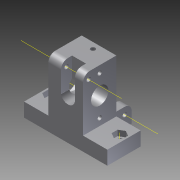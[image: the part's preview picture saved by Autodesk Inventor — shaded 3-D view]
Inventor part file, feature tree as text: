
AUTODESK INVENTOR PART (.ipt)
format: ipt  version: 2012 (Build 160160000, 160)  size: 299,008 bytes
history: native  units: mm
features: hole x11, sketch x10, extrude x7, other x4, fillet x2, plane x1, projected_geometry x1
ambient origin geometry x8: Origin, YZ Plane, XZ Plane, XY Plane, X Axis, Y Axis, Z Axis, Center Point
bodies: Solid1 (feature_tree)
feature tree (36):
  extrude  "Extrusion1"  Depth=24.0mm
  hole  "Hole1"  [1 undecoded]
  hole  "Hole2"  [1 undecoded]
  other  "Work Axis1"
  other  "Work Axis2"
  extrude  "Extrusion2"  Depth=7.5mm
  hole  "Hole3"  [1 undecoded]
  hole  "Hole4"  [1 undecoded]
  extrude  "Extrusion3"  Depth=6.0mm
  hole  "Hole5"  [1 undecoded]
  fillet  "Fillet1"  Radius=12.5mm
  extrude  "Extrusion4"  Depth=13.0mm
  hole  "Hole6"  [1 undecoded]
  hole  "Hole7"  [1 undecoded]
  hole  "Hole8"  [1 undecoded]
  hole  "Hole9"  [1 undecoded]
  hole  "Hole10"  [1 undecoded]
  plane  "Work Plane1"
  extrude  "Extrusion5"  Depth=3.0mm
  extrude  "Extrusion6"  Depth=19.0mm
  extrude  "Extrusion7"  [1 undecoded]
  hole  "Hole11"  [1 undecoded]
  sketch  "Sketch11"  dims[d46=11.0mm d47=25.0mm d48=12.5mm d49=13.0mm d50=13.0mm d51=0.0mm d52=5.0mm d53=6.0mm d54=3.0mm d55=6.0mm d56=4.0mm d57=2.0mm d58=90.0deg d59=0.2mm d60=20.594885mm d61=5.0mm d62=38.0mm d63=0.0mm d64=19.0mm d65=12.0mm d66=12.5mm d67=6.0mm d68=4.0mm d69=2.0mm d70=90.0deg d71=5.1mm d72=20.594885mm d102=10.0mm d103=10.0mm d75=23.0mm d76=6.0mm d77=4.0mm d78=2.0mm d79=90.0deg d80=3.0mm d81=20.594885mm d84=12.0mm d85=5.0mm d86=3.0mm d87=6.0mm d88=4.0mm d89=2.0mm d90=90.0deg d91=0.2mm d92=20.594885mm d93=12.0mm d94=33.0mm d95=3.0mm d96=6.0mm d97=4.0mm d98=2.0mm d99=90.0deg d100=0.2mm d101=20.594885mm d104=8.0mm d105=15.0mm d106=3.0mm d107=19.0mm d108=10.0mm d109=6.0mm d110=4.0mm d111=2.0mm d112=90.0deg d113=10.0mm d114=20.594885mm d115=-8.0mm d116=12.0mm d117=10.0mm d118=0.0mm d119=6.0mm d120=16.0mm d121=10.0mm d122=0.0mm d123=10.0mm d124=8.0mm d125=20.0mm d126=0.0mm d127=4.0mm d128=5.0mm d129=3.0mm d130=6.0mm d131=4.0mm d132=2.0mm d133=90.0deg d134=0.2mm d135=20.594885mm d138=21.0mm d139=5.0mm d140=4.0mm d141=5.0mm d144=1.0mm d145=1.0mm]
  other  "Work Axis3"
  other  "Work Axis4"
  fillet  "Fillet2"  Radius=10.0mm
  sketch  "Sketch1"  dims[d0=60.0mm d1=24.0mm]
  sketch  "Sketch2"  dims[d2=10.0mm d3=0.0mm d4=5.0mm d5=10.0mm]
  sketch  "Sketch3"  dims[d6=4.5mm d7=6.0mm d8=4.0mm d9=2.0mm d10=90.0deg d11=8.0mm d12=20.594885mm d13=5.0mm d14=10.0mm]
  sketch  "Sketch4"  dims[d15=4.5mm d16=6.0mm d17=4.0mm d18=2.0mm d19=90.0deg d20=8.0mm d21=20.594885mm d22=7.5mm]
  sketch  "Sketch5"  dims[d23=7.5mm d24=4.0mm d25=0.0mm]
  sketch  "Sketch6"  dims[d26=4.4mm]
  sketch  "Sketch7"  dims[d27=16.0mm d28=6.0mm d29=4.0mm d30=2.0mm d31=90.0deg d32=5.1mm d33=0.0mm]
  projected_geometry  "Projected Loop1"
  sketch  "Sketch8"  dims[d166=10.0mm d167=10.0mm d36=3.2mm d37=6.0mm d38=4.0mm d39=2.0mm d40=90.0deg d41=0.2mm d42=20.594885mm d43=6.0mm]
  sketch  "Sketch9"  dims[d44=11.0mm d45=6.0mm]
note: 12 required parameter values undecoded (feature->parameter linkage not recoverable at this tier; creation-order binding heuristic only, values carry confidence <= 0.55)
